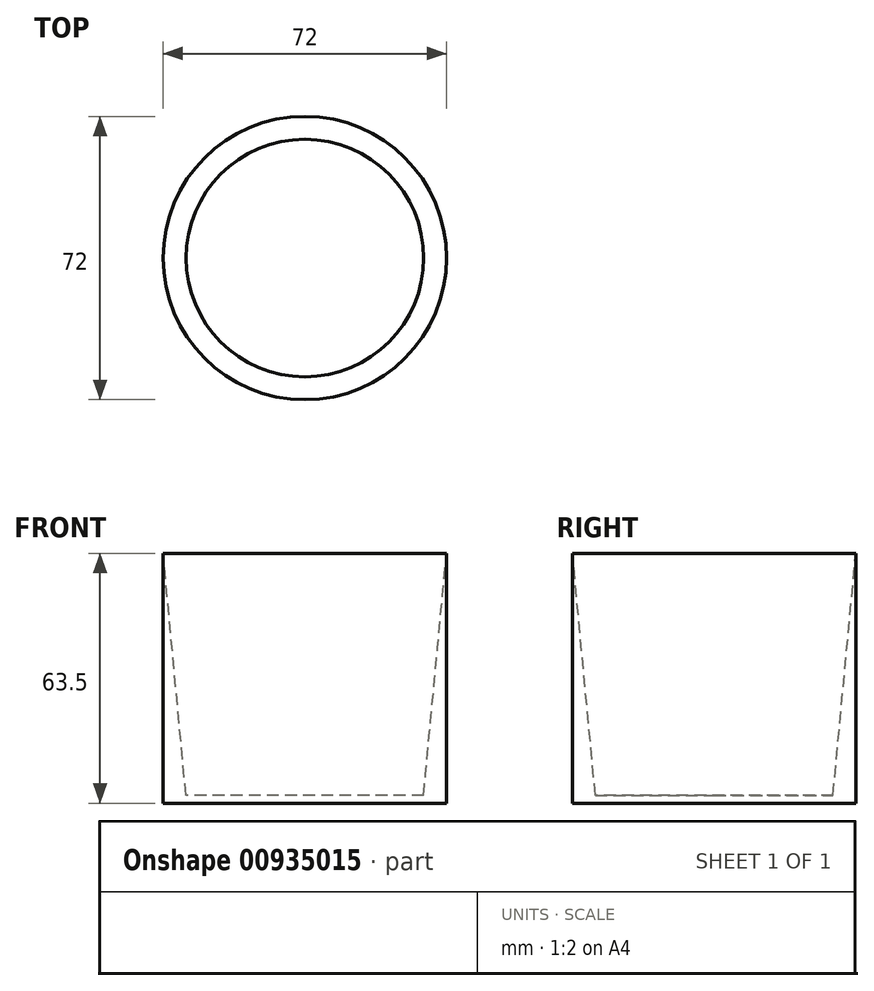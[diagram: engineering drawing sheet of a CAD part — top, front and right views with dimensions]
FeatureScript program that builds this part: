
annotation { "Feature Type Name" : "Feature", "Feature Type Description" : "" }
export const myFeature = defineFeature(function(context is Context, id is Id, definition is map)
    precondition{}
    {
        {
            var Q0;
            Q0=qCreatedBy(makeId("Front.planeOp"),FACE);
            var sketch = newSketch(context, id + "F0", { "sketchPlane" : qUnion([Q0])});
            skLineSegment(sketch, "E0", {"start": v(0, 0) * mm, "end": v(0, 63.5) * mm, "construction": true});
            skSolve(sketch);
        }
        {
            var Q0;
            Q0=qCreatedBy(makeId("Top.planeOp"),FACE);
            var sketch = newSketch(context, id + "F1", { "sketchPlane" : qUnion([Q0])});
            skCircle(sketch, "E1", {"center": v(0, 0) * mm, "radius": 30 * mm});
            skSolve(sketch);
        }
        {
            var Q0;
            Q0=qCreatedBy(makeId("Top.planeOp"),FACE);
            var Q1;
            Q1=sQuery(id+"F0.wireOp",VERTEX,"E0.end");
            cPlane(context, id + "F2", {"entities" : qUnion([Q0, Q1]), "cplaneType" : CPlaneType.PLANE_POINT, "offset" : 25.4 * mm, "width" : 152.4 * mm, "height" : 152.4 * mm});
        }
        {
            var Q0;
            Q0=qCreatedBy(id+"F2.planeOp",FACE);
            var sketch = newSketch(context, id + "F3", { "sketchPlane" : qUnion([Q0])});
            skCircle(sketch, "E2", {"center": v(0, 0) * mm, "radius": 36 * mm});
            skSolve(sketch);
        }
        {
            var Q0;
            Q0 = qSketchRegion(id + "F1", true);
            var Q1;
            Q1 = qSketchRegion(id + "F3", true);
            loft(context, id + "F4", {"sheetProfilesArray" : [{ "sheetProfileEntities" : qUnion([Q0]) }, { "sheetProfileEntities" : qUnion([Q1]) }]});
        }
        {
            var Q0;
            Q0=qCreatedBy(makeId("Top.planeOp"),FACE);
            var sketch = newSketch(context, id + "F5", { "sketchPlane" : qUnion([Q0])});
            skCircle(sketch, "E3", {"center": v(0, 0) * mm, "radius": 36 * mm});
            skSolve(sketch);
        }
        {
            var Q0;
            Q0=makeQuery(id+"F5.imprint","IMPRINT",FACE,{"disambiguationData":[TD([[makeQuery(id+"F5.imprint","IMPRINT",EDGE,{"derivedFrom":sQuery(id+"F5.wireOp",EDGE,"E3")}),1.0]])]});
            var Q1;
            Q1=makeQuery(id+"F4.opLoft","CAP_FACE",FACE,{"disambiguationData":[OSD([makeQuery(id+"F3.imprint","IMPRINT",FACE,{"disambiguationData":[TD([[makeQuery(id+"F3.imprint","IMPRINT",EDGE,{"derivedFrom":sQuery(id+"F3.wireOp",EDGE,"E2")}),1.0]])]})])],"isStart":true});
            extrude(context, id + "F6", {"entities" : qUnion([Q0]), "endBound" : BoundingType.UP_TO_SURFACE, "depth" : 25.4 * mm, "endBoundEntityFace" : qUnion([Q1]), "offsetDistance" : 25.4 * mm});
        }
        {
            var Q0;
            Q0=makeQuery(id+"F4.opLoft","SWEPT_BODY",BODY,{"disambiguationData":[OSD([makeQuery(id+"F1.imprint","IMPRINT",FACE,{"disambiguationData":[TD([[makeQuery(id+"F1.imprint","IMPRINT",EDGE,{"derivedFrom":sQuery(id+"F1.wireOp",EDGE,"E1")}),1.0]])]}),makeQuery(id+"F3.imprint","IMPRINT",FACE,{"disambiguationData":[TD([[makeQuery(id+"F3.imprint","IMPRINT",EDGE,{"derivedFrom":sQuery(id+"F3.wireOp",EDGE,"E2")}),1.0]])]})])]});
            var Q1;
            Q1=makeQuery(id+"F6.opExtrude","SWEPT_BODY",BODY,{"disambiguationData":[OSD([sQuery(id+"F5.wireOp",EDGE,"E3")])]});
            booleanBodies(context, id + "F7", {"operationType" : BooleanOperationType.SUBTRACTION, "tools" : qUnion([Q0]), "targets" : qUnion([Q1])});
        }
        {
            var Q0;
            Q0=makeQuery(id+"F5.imprint","IMPRINT",FACE,{"disambiguationData":[TD([[makeQuery(id+"F5.imprint","IMPRINT",EDGE,{"derivedFrom":sQuery(id+"F5.wireOp",EDGE,"E3")}),1.0]])]});
            extrude(context, id + "F8", {"entities" : qUnion([Q0]), "operationType" : NewBodyOperationType.ADD, "depth" : 2 * mm, "offsetDistance" : 25.4 * mm});
        }
    });
